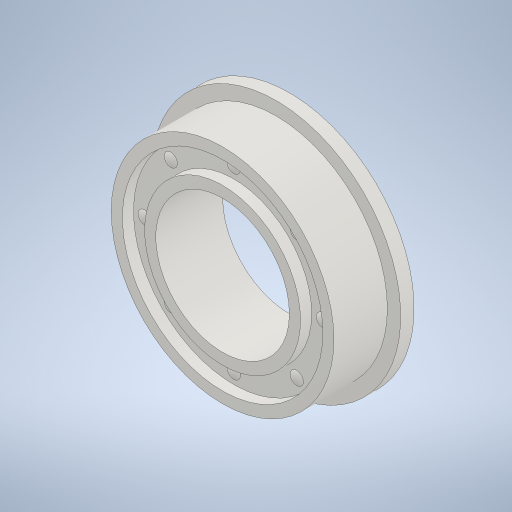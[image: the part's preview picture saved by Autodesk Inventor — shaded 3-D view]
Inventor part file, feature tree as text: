
AUTODESK INVENTOR PART (.ipt)
format: ipt  version: 2023 (Build 270158030, 158C)  size: 336,896 bytes
history: native  units: mm
features: sketch x7, other x4, extrude x4, revolve x1, pattern_circular x1
ambient origin geometry x8: Origin, YZ Plane, XZ Plane, XY Plane, X Axis, Y Axis, Z Axis, Center Point
bodies: Body1 (feature_tree)
feature tree (17):
  other  "ソリッド1"
  extrude  "押し出し1"  Depth=6.0mm
  sketch  "スケッチ2"
  other  "作業平面1"
  other  "作業平面2"
  other  "作業平面3"
  revolve  "回転1"
  pattern_circular  "円形状パターン1"  [2 undecoded]
  extrude  "押し出し2"  Depth=10.0mm
  extrude  "押し出し3"  Depth=9.0mm
  extrude  "押し出し4"  Depth=2.4mm TaperAngle=0.0deg
  sketch  "スケッチ7"
  sketch  "スケッチ1"
  sketch  "スケッチ3"
  sketch  "スケッチ4"
  sketch  "スケッチ5"
  sketch  "スケッチ6"
note: 2 required parameter values undecoded (feature->parameter linkage not recoverable at this tier; creation-order binding heuristic only, values carry confidence <= 0.55)
